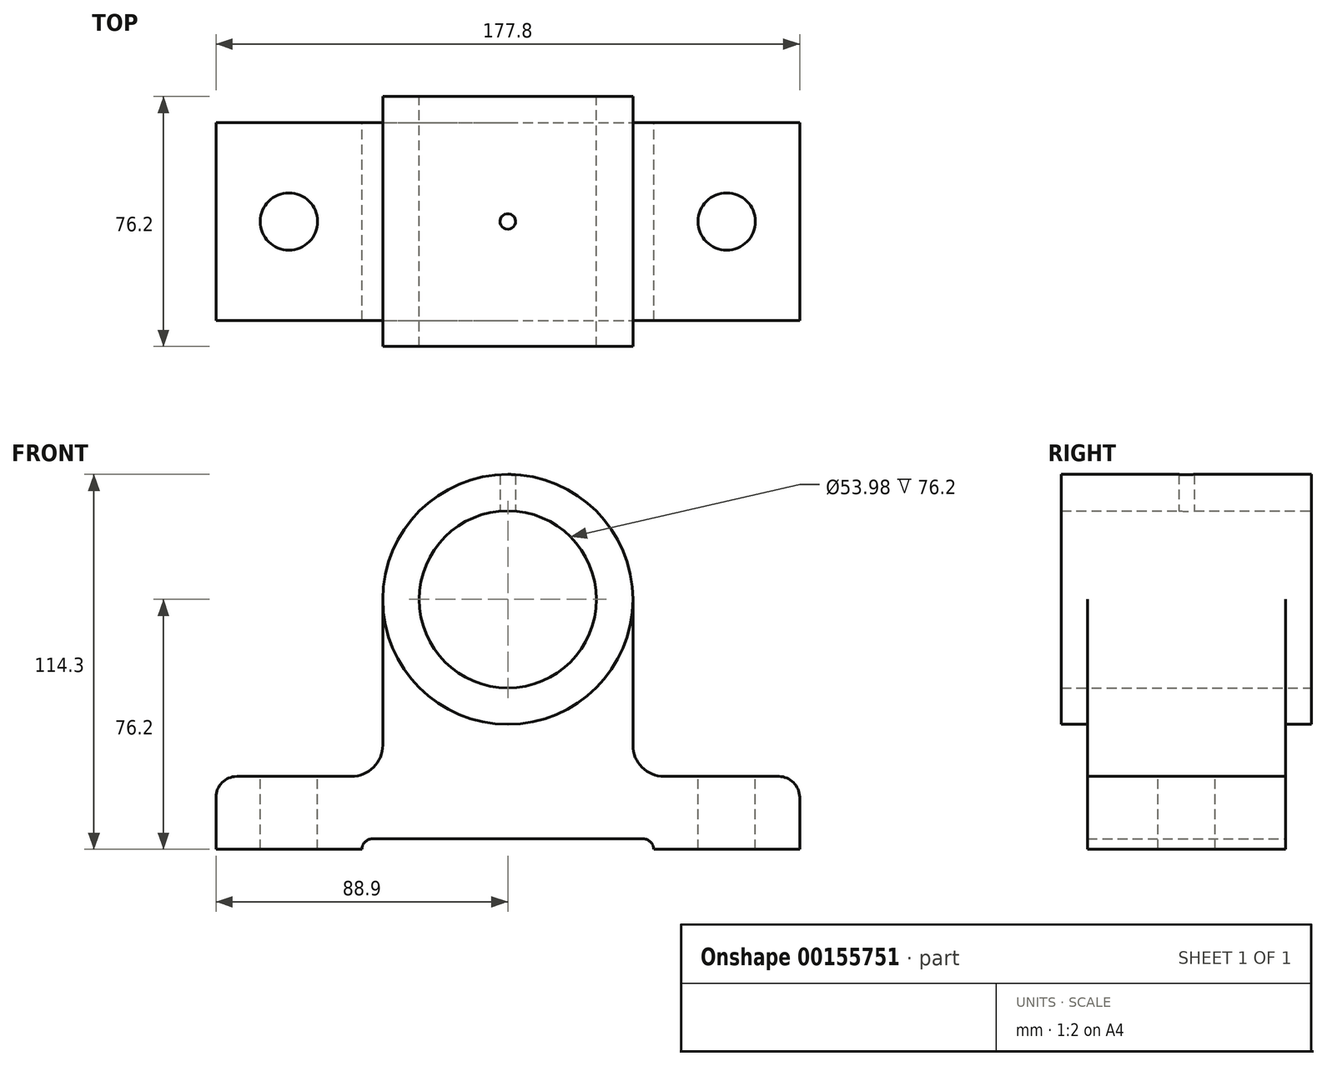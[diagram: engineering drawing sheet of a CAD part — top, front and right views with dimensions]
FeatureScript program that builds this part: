
annotation { "Feature Type Name" : "Feature", "Feature Type Description" : "" }
export const myFeature = defineFeature(function(context is Context, id is Id, definition is map)
    precondition{}
    {
        {
            var Q0;
            Q0=qCreatedBy(makeId("Front.planeOp"),FACE);
            var sketch = newSketch(context, id + "F0", { "sketchPlane" : qUnion([Q0])});
            skCircle(sketch, "E0", {"center": v(0, 0) * mm, "radius": 38.1 * mm});
            skLineSegment(sketch, "E1", {"start": v(-38.1, 0) * mm, "end": v(-38.1, -53.97) * mm});
            skLineSegment(sketch, "E2", {"start": v(-38.1, -53.97) * mm, "end": v(-88.9, -53.97) * mm});
            skLineSegment(sketch, "E3", {"start": v(-88.9, -53.97) * mm, "end": v(-88.9, -76.2) * mm});
            skLineSegment(sketch, "E4", {"start": v(-88.9, -76.2) * mm, "end": v(-44.45, -76.2) * mm});
            skLineSegment(sketch, "E5", {"start": v(0, -76.2) * mm, "end": v(0, 64.1) * mm, "construction": true});
            skLineSegment(sketch, "E6", {"start": v(-44.45, -76.2) * mm, "end": v(-44.45, -73.03) * mm});
            skLineSegment(sketch, "E7", {"start": v(-44.45, -73.03) * mm, "end": v(0, -73.03) * mm});
            skLineSegment(sketch, "E8.MirrorCS", {"start": v(44.45, -73.03) * mm, "end": v(0, -73.03) * mm});
            skLineSegment(sketch, "E9.MirrorCS", {"start": v(44.45, -76.2) * mm, "end": v(44.45, -73.03) * mm});
            skLineSegment(sketch, "E10.MirrorCS", {"start": v(88.9, -76.2) * mm, "end": v(44.45, -76.2) * mm});
            skLineSegment(sketch, "E11.MirrorCS", {"start": v(38.1, -53.97) * mm, "end": v(88.9, -53.97) * mm});
            skLineSegment(sketch, "E12.MirrorCS", {"start": v(38.1, 0) * mm, "end": v(38.1, -53.97) * mm});
            skLineSegment(sketch, "E13.MirrorCS", {"start": v(88.9, -53.97) * mm, "end": v(88.9, -76.2) * mm});
            skCircle(sketch, "E14", {"center": v(0, 0) * mm, "radius": 26.99 * mm});
            skSolve(sketch);
        }
        {
            var Q0;
            Q0=makeQuery(id+"F0.imprint","IMPRINT",FACE,{"disambiguationData":[TD([[makeQuery(id+"F0.imprint","IMPRINT",EDGE,{"derivedFrom":sQuery(id+"F0.wireOp",EDGE,"E14")}),-1.0]])]});
            extrude(context, id + "F1", {"entities" : qUnion([Q0]), "depth" : 76.2 * mm, "symmetric" : true});
        }
        {
            var Q0;
            Q0 = qSketchRegion(id + "F0", true);
            extrude(context, id + "F2", {"entities" : qUnion([Q0]), "operationType" : NewBodyOperationType.ADD, "depth" : 60.32 * mm, "symmetric" : true});
        }
        {
            var Q0;
            Q0=qCreatedBy(makeId("Top.planeOp"),FACE);
            var sketch = newSketch(context, id + "F3", { "sketchPlane" : qUnion([Q0])});
            skLineSegment(sketch, "E15", {"start": v(0, 83.57) * mm, "end": v(0, -78.09) * mm, "construction": true});
            skCircle(sketch, "E16", {"center": v(-66.67, 0) * mm, "radius": 8.73 * mm});
            skCircle(sketch, "E17.MirrorC", {"center": v(66.68, 0) * mm, "radius": 8.73 * mm});
            skSolve(sketch);
        }
        {
            var Q0;
            Q0 = qSketchRegion(id + "F3", true);
            extrude(context, id + "F4", {"entities" : qUnion([Q0]), "operationType" : NewBodyOperationType.REMOVE, "endBound" : BoundingType.THROUGH_ALL, "oppositeDirection" : true, "depth" : 25.4 * mm});
        }
        {
            var Q0;
            Q0=qCreatedBy(makeId("Top.planeOp"),FACE);
            var sketch = newSketch(context, id + "F5", { "sketchPlane" : qUnion([Q0])});
            skCircle(sketch, "E18", {"center": v(0, 0) * mm, "radius": 2.38 * mm});
            skSolve(sketch);
        }
        {
            var Q0;
            Q0 = qSketchRegion(id + "F5", true);
            extrude(context, id + "F6", {"entities" : qUnion([Q0]), "operationType" : NewBodyOperationType.REMOVE, "endBound" : BoundingType.THROUGH_ALL, "depth" : 25.4 * mm});
        }
        {
            var Q0;
            Q0=makeQuery(id+"F2.opExtrude","SWEPT_EDGE",EDGE,{"disambiguationData":[OSD([sQuery(id+"F0.wireOp",EDGE,"E11.MirrorCS"),sQuery(id+"F0.wireOp",EDGE,"E12.MirrorCS")])]});
            var Q1;
            Q1=makeQuery(id+"F2.opExtrude","SWEPT_EDGE",EDGE,{"disambiguationData":[OSD([sQuery(id+"F0.wireOp",EDGE,"E1"),sQuery(id+"F0.wireOp",EDGE,"E2")])]});
            fillet(context, id + "F7", {"entities" : qUnion([Q0, Q1]), "radius" : 9.52 * mm, "tangentPropagation" : true, "allowEdgeOverflow" : false});
        }
        {
            var Q0;
            Q0=makeQuery(id+"F2.opExtrude","SWEPT_EDGE",EDGE,{"disambiguationData":[OSD([sQuery(id+"F0.wireOp",EDGE,"E2"),sQuery(id+"F0.wireOp",EDGE,"E3")])]});
            var Q1;
            Q1=makeQuery(id+"F2.opExtrude","SWEPT_EDGE",EDGE,{"disambiguationData":[OSD([sQuery(id+"F0.wireOp",EDGE,"E11.MirrorCS"),sQuery(id+"F0.wireOp",EDGE,"E13.MirrorCS")])]});
            fillet(context, id + "F8", {"entities" : qUnion([Q0, Q1]), "radius" : 6.35 * mm, "tangentPropagation" : true, "allowEdgeOverflow" : false});
        }
        {
            var Q0;
            Q0=makeQuery(id+"F2.opExtrude","SWEPT_EDGE",EDGE,{"disambiguationData":[OSD([sQuery(id+"F0.wireOp",EDGE,"E6"),sQuery(id+"F0.wireOp",EDGE,"E7")])]});
            var Q1;
            Q1=makeQuery(id+"F2.opExtrude","SWEPT_EDGE",EDGE,{"disambiguationData":[OSD([sQuery(id+"F0.wireOp",EDGE,"E8.MirrorCS"),sQuery(id+"F0.wireOp",EDGE,"E9.MirrorCS")])]});
            fillet(context, id + "F9", {"entities" : qUnion([Q0, Q1]), "radius" : 3.17 * mm, "tangentPropagation" : true, "allowEdgeOverflow" : false});
        }
    });
